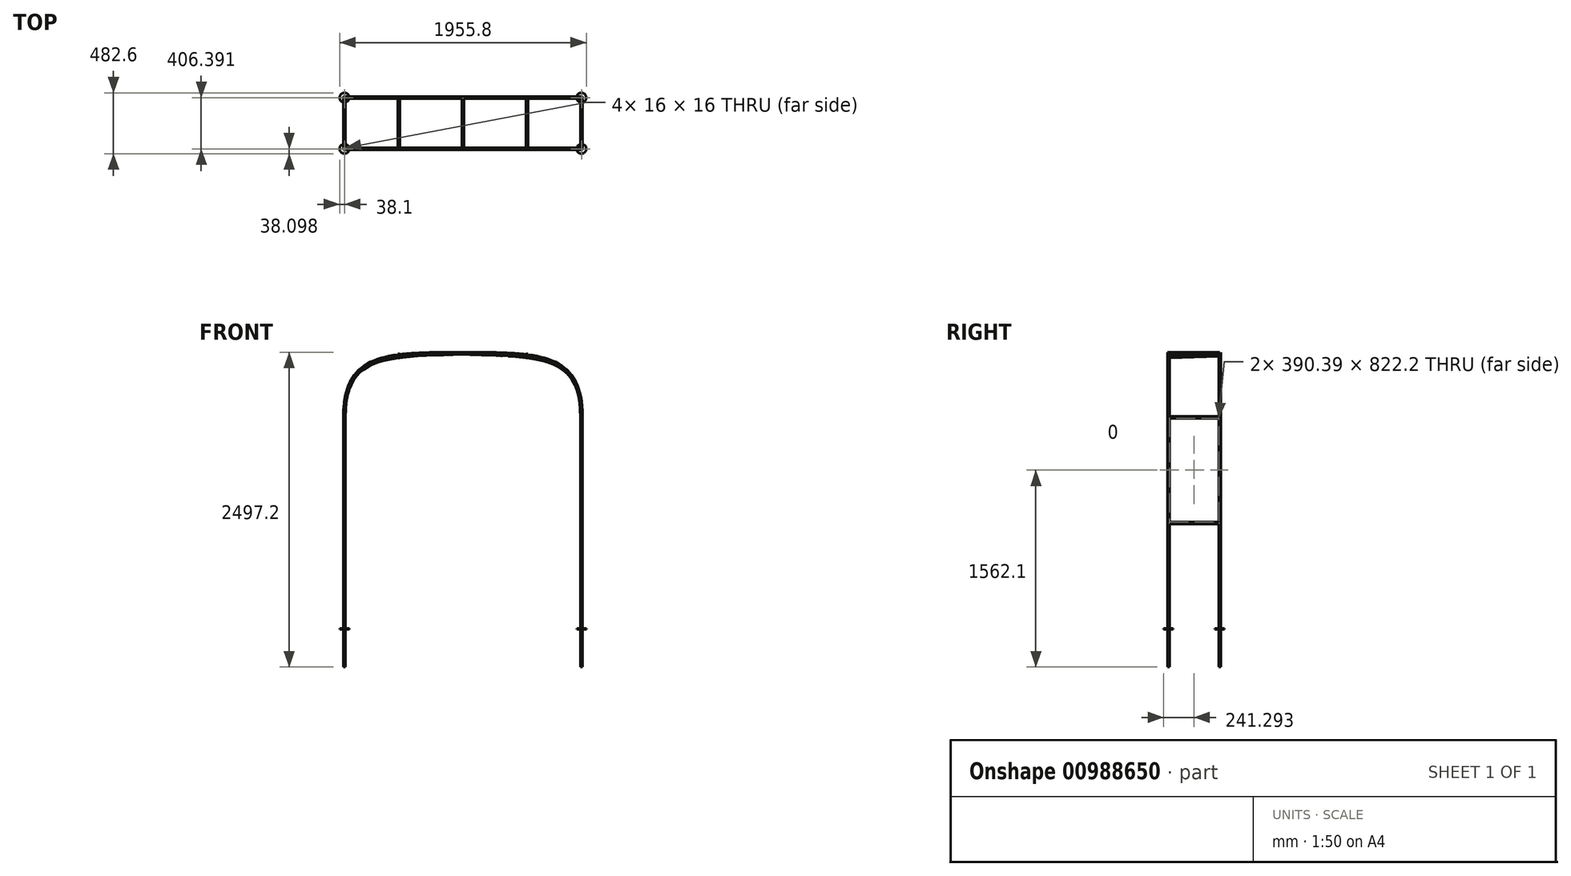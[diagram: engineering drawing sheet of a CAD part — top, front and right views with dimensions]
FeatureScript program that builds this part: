
annotation { "Feature Type Name" : "Feature", "Feature Type Description" : "" }
export const myFeature = defineFeature(function(context is Context, id is Id, definition is map)
    precondition{}
    {
        {
            var Q0;
            Q0=qCreatedBy(makeId("Right.planeOp"),FACE);
            cPlane(context, id + "F0", {"entities" : qUnion([Q0]), "cplaneType" : CPlaneType.OFFSET, "offset" : 939.8 * mm, "oppositeDirection" : true, "width" : 152.4 * mm, "height" : 152.4 * mm});
        }
        {
            var Q0;
            Q0=qCreatedBy(id+"F0.planeOp",FACE);
            var sketch = newSketch(context, id + "F1", { "sketchPlane" : qUnion([Q0])});
            skLineSegment(sketch, "E0", {"start": v(0, 0) * mm, "end": v(-203.2, 0) * mm, "construction": true});
            skLineSegment(sketch, "E1", {"start": v(0, 0) * mm, "end": v(203.2, 0) * mm, "construction": true});
            skLineSegment(sketch, "E2", {"start": v(203.2, 0) * mm, "end": v(203.2, 2184.4) * mm, "construction": true});
            skLineSegment(sketch, "E3", {"start": v(203.2, 2184.4) * mm, "end": v(-203.2, 2184.4) * mm, "construction": true});
            skLineSegment(sketch, "E4", {"start": v(-203.2, 2184.4) * mm, "end": v(-203.2, 0) * mm, "construction": true});
            skSolve(sketch);
        }
        {
            var Q0;
            Q0=qCreatedBy(makeId("Right.planeOp"),FACE);
            var sketch = newSketch(context, id + "F2", { "sketchPlane" : qUnion([Q0])});
            skPoint(sketch, "E5.0", {"position": v(0, 2184.4) * mm});
            skLineSegment(sketch, "E6.0", {"start": v(-203.2, 2184.4) * mm, "end": v(-203.2, 0) * mm, "construction": true});
            skLineSegment(sketch, "E7.0", {"start": v(203.2, 0) * mm, "end": v(203.2, 2184.4) * mm, "construction": true});
            skSolve(sketch);
        }
        {
            var Q0;
            Q0=qCreatedBy(id+"F0.planeOp",FACE);
            var sketch = newSketch(context, id + "F3", { "sketchPlane" : qUnion([Q0])});
            skLineSegment(sketch, "E8", {"start": v(-203.2, 0) * mm, "end": v(-203.2, 1676.4) * mm});
            skLineSegment(sketch, "E9", {"start": v(203.19, 0) * mm, "end": v(203.19, 1676.4) * mm});
            skSolve(sketch);
        }
        {
            var Q0;
            Q0=sQuery(id+"F1.wireOp",EDGE,"E4");
            cPlane(context, id + "F4", {"entities" : qUnion([Q0]), "cplaneType" : CPlaneType.LINE_ANGLE, "offset" : 25.4 * mm, "angle" : 90 * degree, "width" : 152.4 * mm, "height" : 152.4 * mm});
        }
        {
            var Q0;
            Q0=sQuery(id+"F1.wireOp",EDGE,"E2");
            cPlane(context, id + "F5", {"entities" : qUnion([Q0]), "cplaneType" : CPlaneType.LINE_ANGLE, "offset" : 25.4 * mm, "angle" : 90 * degree, "width" : 152.4 * mm, "height" : 152.4 * mm});
        }
        {
            var Q0;
            Q0=qCreatedBy(id+"F4.planeOp",FACE);
            var sketch = newSketch(context, id + "F6", { "sketchPlane" : qUnion([Q0])});
            skFitSpline(sketch, "E10", {"points": [v(940.37, 1675.96) * mm, v(0, 2184.4) * mm], "startDerivative": vector(-2.6, 1524) * mm, "endDerivative": vector(-1828.8, 68.52) * mm});
            skLineSegment(sketch, "E11", {"start": v(609.6, 2161.56) * mm, "end": v(0, 2184.4) * mm, "construction": true});
            skLineSegment(sketch, "E12", {"start": v(940.37, 1675.96) * mm, "end": v(939.5, 2183.96) * mm, "construction": true});
            skSolve(sketch);
        }
        {
            var Q0;
            Q0=qCreatedBy(id+"F5.planeOp",FACE);
            var sketch = newSketch(context, id + "F7", { "sketchPlane" : qUnion([Q0])});
            skFitSpline(sketch, "E13", {"points": [v(939.8, 1676.4) * mm, v(0, 2184.4) * mm], "startDerivative": vector(4.32, 1524) * mm, "endDerivative": vector(-1828.8, 1.65) * mm});
            skLineSegment(sketch, "E14", {"start": v(939.8, 1676.4) * mm, "end": v(941.24, 2184.4) * mm, "construction": true});
            skLineSegment(sketch, "E15", {"start": v(0, 2184.4) * mm, "end": v(609.6, 2183.85) * mm, "construction": true});
            skSolve(sketch);
        }
        {
            var Q0;
            Q0=qCreatedBy(makeId("Top.planeOp"),FACE);
            var sketch = newSketch(context, id + "F8", { "sketchPlane" : qUnion([Q0])});
            skLineSegment(sketch, "E16.bottom", {"start": v(-947.8, -195.2) * mm, "end": v(-931.8, -195.2) * mm});
            skLineSegment(sketch, "E16.top", {"start": v(-947.8, -211.2) * mm, "end": v(-931.8, -211.2) * mm});
            skLineSegment(sketch, "E16.left", {"start": v(-947.8, -195.2) * mm, "end": v(-947.8, -211.2) * mm});
            skLineSegment(sketch, "E16.right", {"start": v(-931.8, -195.2) * mm, "end": v(-931.8, -211.2) * mm});
            skLineSegment(sketch, "E17", {"start": v(-947.8, -195.2) * mm, "end": v(-931.8, -211.2) * mm, "construction": true});
            skPoint(sketch, "E18", {"position": v(-939.8, -203.2) * mm});
            skLineSegment(sketch, "E19.bottom", {"start": v(-931.8, 211.19) * mm, "end": v(-947.8, 211.19) * mm});
            skLineSegment(sketch, "E19.top", {"start": v(-931.8, 195.19) * mm, "end": v(-947.8, 195.19) * mm});
            skLineSegment(sketch, "E19.left", {"start": v(-931.8, 211.19) * mm, "end": v(-931.8, 195.19) * mm});
            skLineSegment(sketch, "E19.right", {"start": v(-947.8, 211.19) * mm, "end": v(-947.8, 195.19) * mm});
            skLineSegment(sketch, "E20", {"start": v(-931.8, 211.19) * mm, "end": v(-947.8, 195.19) * mm, "construction": true});
            skPoint(sketch, "E21", {"position": v(-939.8, 203.19) * mm});
            skSolve(sketch);
        }
        {
            var Q0;
            Q0=makeQuery(id+"F8.imprint","IMPRINT",FACE,{"disambiguationData":[TD([[makeQuery(id+"F8.imprint","IMPRINT",EDGE,{"derivedFrom":sQuery(id+"F8.wireOp",EDGE,"E19.bottom")}),1.0]])]});
            var Q1;
            Q1=sQuery(id+"F3.wireOp",EDGE,"E9");
            sweep(context, id + "F9", {"profiles" : qUnion([Q0]), "path" : qUnion([Q1])});
        }
        {
            var Q0;
            Q0=makeQuery(id+"F8.imprint","IMPRINT",FACE,{"disambiguationData":[TD([[makeQuery(id+"F8.imprint","IMPRINT",EDGE,{"derivedFrom":sQuery(id+"F8.wireOp",EDGE,"E16.bottom")}),-1.0]])]});
            var Q1;
            Q1=sQuery(id+"F3.wireOp",EDGE,"E8");
            sweep(context, id + "F10", {"profiles" : qUnion([Q0]), "path" : qUnion([Q1])});
        }
        {
            var Q0;
            Q0=makeQuery(id+"F10.opSweep","CAP_FACE",FACE,{"disambiguationData":[OSD([sQuery(id+"F3.wireOp",VERTEX,"E8.end"),sQuery(id+"F8.wireOp",EDGE,"dGPdL38b-pFhj-TtEV-cKe8-G57E5a3NYJfa")])],"isStart":false});
            var Q1;
            Q1=sQuery(id+"F6.wireOp",EDGE,"E10");
            sweep(context, id + "F11", {"operationType" : NewBodyOperationType.ADD, "profiles" : qUnion([Q0]), "path" : qUnion([Q1])});
        }
        {
            var Q0;
            Q0=qCreatedBy(id+"F0.planeOp",FACE);
            var sketch = newSketch(context, id + "F12", { "sketchPlane" : qUnion([Q0])});
            skLineSegment(sketch, "E22", {"start": v(203.19, 838.2) * mm, "end": v(-203.2, 838.2) * mm});
            skSolve(sketch);
        }
        {
            var Q0;
            Q0=qCreatedBy(id+"F0.planeOp",FACE);
            var sketch = newSketch(context, id + "F13", { "sketchPlane" : qUnion([Q0])});
            skLineSegment(sketch, "E23", {"start": v(-203.2, 1676.4) * mm, "end": v(203.19, 1676.4) * mm});
            skSolve(sketch);
        }
        {
            var Q0;
            Q0=makeQuery(id+"F9.opSweep","CAP_FACE",FACE,{"disambiguationData":[OSD([sQuery(id+"F3.wireOp",VERTEX,"E9.end"),sQuery(id+"F8.wireOp",EDGE,"A7kbO7hZ-qHPU-M1P2-TBv8-yGFhnXoMKm63")])],"isStart":false});
            var Q1;
            Q1=sQuery(id+"F7.wireOp",EDGE,"E13");
            sweep(context, id + "F14", {"operationType" : NewBodyOperationType.ADD, "profiles" : qUnion([Q0]), "path" : qUnion([Q1])});
        }
        {
            var Q0;
            Q0=qCreatedBy(makeId("Right.planeOp"),FACE);
            var sketch = newSketch(context, id + "F15", { "sketchPlane" : qUnion([Q0])});
            skLineSegment(sketch, "E24", {"start": v(-203.2, 2184.4) * mm, "end": v(203.2, 2184.4) * mm});
            skSolve(sketch);
        }
        {
            var Q0;
            Q0=qCreatedBy(id+"F4.planeOp",FACE);
            var sketch = newSketch(context, id + "F16", { "sketchPlane" : qUnion([Q0])});
            skCircle(sketch, "E25", {"center": v(939.8, 838.2) * mm, "radius": 8 * mm});
            skCircle(sketch, "E26", {"center": v(939.8, 1676.4) * mm, "radius": 8 * mm});
            skLineSegment(sketch, "E27.bottom", {"start": v(947.8, 830.2) * mm, "end": v(931.8, 830.2) * mm});
            skLineSegment(sketch, "E27.top", {"start": v(947.8, 846.2) * mm, "end": v(931.8, 846.2) * mm});
            skLineSegment(sketch, "E27.left", {"start": v(947.8, 830.2) * mm, "end": v(947.8, 846.2) * mm});
            skLineSegment(sketch, "E27.right", {"start": v(931.8, 830.2) * mm, "end": v(931.8, 846.2) * mm});
            skLineSegment(sketch, "E28", {"start": v(947.8, 830.2) * mm, "end": v(931.8, 846.2) * mm, "construction": true});
            skLineSegment(sketch, "E29.bottom", {"start": v(947.8, 1684.4) * mm, "end": v(931.8, 1684.4) * mm});
            skLineSegment(sketch, "E29.top", {"start": v(947.8, 1668.4) * mm, "end": v(931.8, 1668.4) * mm});
            skLineSegment(sketch, "E29.left", {"start": v(947.8, 1684.4) * mm, "end": v(947.8, 1668.4) * mm});
            skLineSegment(sketch, "E29.right", {"start": v(931.8, 1684.4) * mm, "end": v(931.8, 1668.4) * mm});
            skLineSegment(sketch, "E30", {"start": v(947.8, 1668.4) * mm, "end": v(931.8, 1684.4) * mm, "construction": true});
            skSolve(sketch);
        }
        {
            var Q0;
            Q0=makeQuery(id+"F16.imprint","IMPRINT",FACE,{"disambiguationData":[TD([[makeQuery(id+"F16.imprint","IMPRINT",EDGE,{"derivedFrom":sQuery(id+"F16.wireOp",EDGE,"E25")}),1.0]])]});
            var Q1;
            Q1=sQuery(id+"F12.wireOp",EDGE,"E22");
            sweep(context, id + "F17", {"operationType" : NewBodyOperationType.ADD, "profiles" : qUnion([Q0]), "path" : qUnion([Q1])});
        }
        {
            var Q0;
            Q0=qSketchRegion(id+"F16",true);
            var Q1;
            Q1=sQuery(id+"F13.wireOp",EDGE,"E23");
            sweep(context, id + "F18", {"operationType" : NewBodyOperationType.ADD, "profiles" : qUnion([Q0]), "path" : qUnion([Q1])});
        }
        {
            var Q0;
            Q0=qCreatedBy(id+"F4.planeOp",FACE);
            var sketch = newSketch(context, id + "F19", { "sketchPlane" : qUnion([Q0])});
            skLineSegment(sketch, "E31", {"start": v(8, 2176.4) * mm, "end": v(-8, 2192.4) * mm, "construction": true});
            skPoint(sketch, "E32", {"position": v(0, 2184.4) * mm});
            skLineSegment(sketch, "E33.bottom", {"start": v(8, 2176.4) * mm, "end": v(-8, 2176.4) * mm});
            skLineSegment(sketch, "E33.top", {"start": v(8, 2192.4) * mm, "end": v(-8, 2192.4) * mm});
            skLineSegment(sketch, "E33.left", {"start": v(8, 2176.4) * mm, "end": v(8, 2192.4) * mm});
            skLineSegment(sketch, "E33.right", {"start": v(-8, 2176.4) * mm, "end": v(-8, 2192.4) * mm});
            skSolve(sketch);
        }
        {
            var Q0;
            Q0=makeQuery(id+"F19.imprint","IMPRINT",FACE,{"disambiguationData":[TD([[makeQuery(id+"F19.imprint","IMPRINT",EDGE,{"derivedFrom":sQuery(id+"F19.wireOp",EDGE,"E33.bottom")}),-1.0]])]});
            var Q1;
            Q1=sQuery(id+"F15.wireOp",EDGE,"E24");
            sweep(context, id + "F20", {"operationType" : NewBodyOperationType.ADD, "profiles" : qUnion([Q0]), "path" : qUnion([Q1])});
        }
        {
            var Q0;
            Q0=qCreatedBy(makeId("Right.planeOp"),FACE);
            cPlane(context, id + "F21", {"entities" : qUnion([Q0]), "cplaneType" : CPlaneType.OFFSET, "offset" : 508 * mm, "oppositeDirection" : true, "width" : 152.4 * mm, "height" : 152.4 * mm});
        }
        {
            var Q0;
            Q0=qCreatedBy(id+"F21.planeOp",FACE);
            var sketch = newSketch(context, id + "F22", { "sketchPlane" : qUnion([Q0])});
            skLineSegment(sketch, "E34", {"start": v(-203.2, 2154.74) * mm, "end": v(203.2, 2169.14) * mm});
            skSolve(sketch);
        }
        {
            var Q0;
            Q0=qCreatedBy(id+"F4.planeOp",FACE);
            var sketch = newSketch(context, id + "F23", { "sketchPlane" : qUnion([Q0])});
            skCircle(sketch, "E35", {"center": v(508, 2154.74) * mm, "radius": 7.62 * mm});
            skLineSegment(sketch, "E36.bottom", {"start": v(516, 2162.74) * mm, "end": v(500, 2162.74) * mm});
            skLineSegment(sketch, "E36.top", {"start": v(516, 2146.74) * mm, "end": v(500, 2146.74) * mm});
            skLineSegment(sketch, "E36.left", {"start": v(516, 2162.74) * mm, "end": v(516, 2146.74) * mm});
            skLineSegment(sketch, "E36.right", {"start": v(500, 2162.74) * mm, "end": v(500, 2146.74) * mm});
            skLineSegment(sketch, "E37", {"start": v(516, 2146.74) * mm, "end": v(500, 2162.74) * mm, "construction": true});
            skSolve(sketch);
        }
        {
            var Q0;
            Q0=qSketchRegion(id+"F23",true);
            var Q1;
            Q1=sQuery(id+"F22.wireOp",EDGE,"E34");
            sweep(context, id + "F24", {"operationType" : NewBodyOperationType.ADD, "profiles" : qUnion([Q0]), "path" : qUnion([Q1])});
        }
        {
            var Q0;
            Q0=qCreatedBy(makeId("Top.planeOp"),FACE);
            var sketch = newSketch(context, id + "F25", { "sketchPlane" : qUnion([Q0])});
            skCircle(sketch, "E38", {"center": v(-939.8, -203.2) * mm, "radius": 38.1 * mm});
            skCircle(sketch, "E39", {"center": v(-939.8, 203.2) * mm, "radius": 38.1 * mm});
            skSolve(sketch);
        }
        {
            var Q0;
            Q0=qSketchRegion(id+"F25",true);
            extrude(context, id + "F26", {"entities" : qUnion([Q0]), "operationType" : NewBodyOperationType.ADD, "oppositeDirection" : true, "depth" : 6.35 * mm, "offsetDistance" : 25.4 * mm});
        }
        {
            var Q0;
            Q0=makeQuery(id+"F8.imprint","IMPRINT",FACE,{"disambiguationData":[TD([[makeQuery(id+"F8.imprint","IMPRINT",EDGE,{"derivedFrom":sQuery(id+"F8.wireOp",EDGE,"E16.bottom")}),-1.0]])]});
            extrude(context, id + "F27", {"entities" : qUnion([Q0]), "operationType" : NewBodyOperationType.ADD, "oppositeDirection" : true, "depth" : 304.8 * mm, "offsetDistance" : 25.4 * mm});
        }
        {
            var Q0;
            Q0=makeQuery(id+"F8.imprint","IMPRINT",FACE,{"disambiguationData":[TD([[makeQuery(id+"F8.imprint","IMPRINT",EDGE,{"derivedFrom":sQuery(id+"F8.wireOp",EDGE,"E19.bottom")}),1.0]])]});
            extrude(context, id + "F28", {"entities" : qUnion([Q0]), "operationType" : NewBodyOperationType.ADD, "oppositeDirection" : true, "depth" : 304.8 * mm, "offsetDistance" : 25.4 * mm});
        }
        {
            var Q0;
            Q0=makeQuery(id+"F9.opSweep","SWEPT_BODY",BODY,{"disambiguationData":[OSD([sQuery(id+"F3.wireOp",EDGE,"E9"),sQuery(id+"F8.wireOp",EDGE,"A7kbO7hZ-qHPU-M1P2-TBv8-yGFhnXoMKm63")])]});
            var Q1;
            Q1=qCreatedBy(makeId("Right.planeOp"),FACE);
            mirror(context, id + "F29", {"operationType" : NewBodyOperationType.ADD, "entities" : qUnion([Q0]), "mirrorPlane" : qUnion([Q1])});
        }
    });
